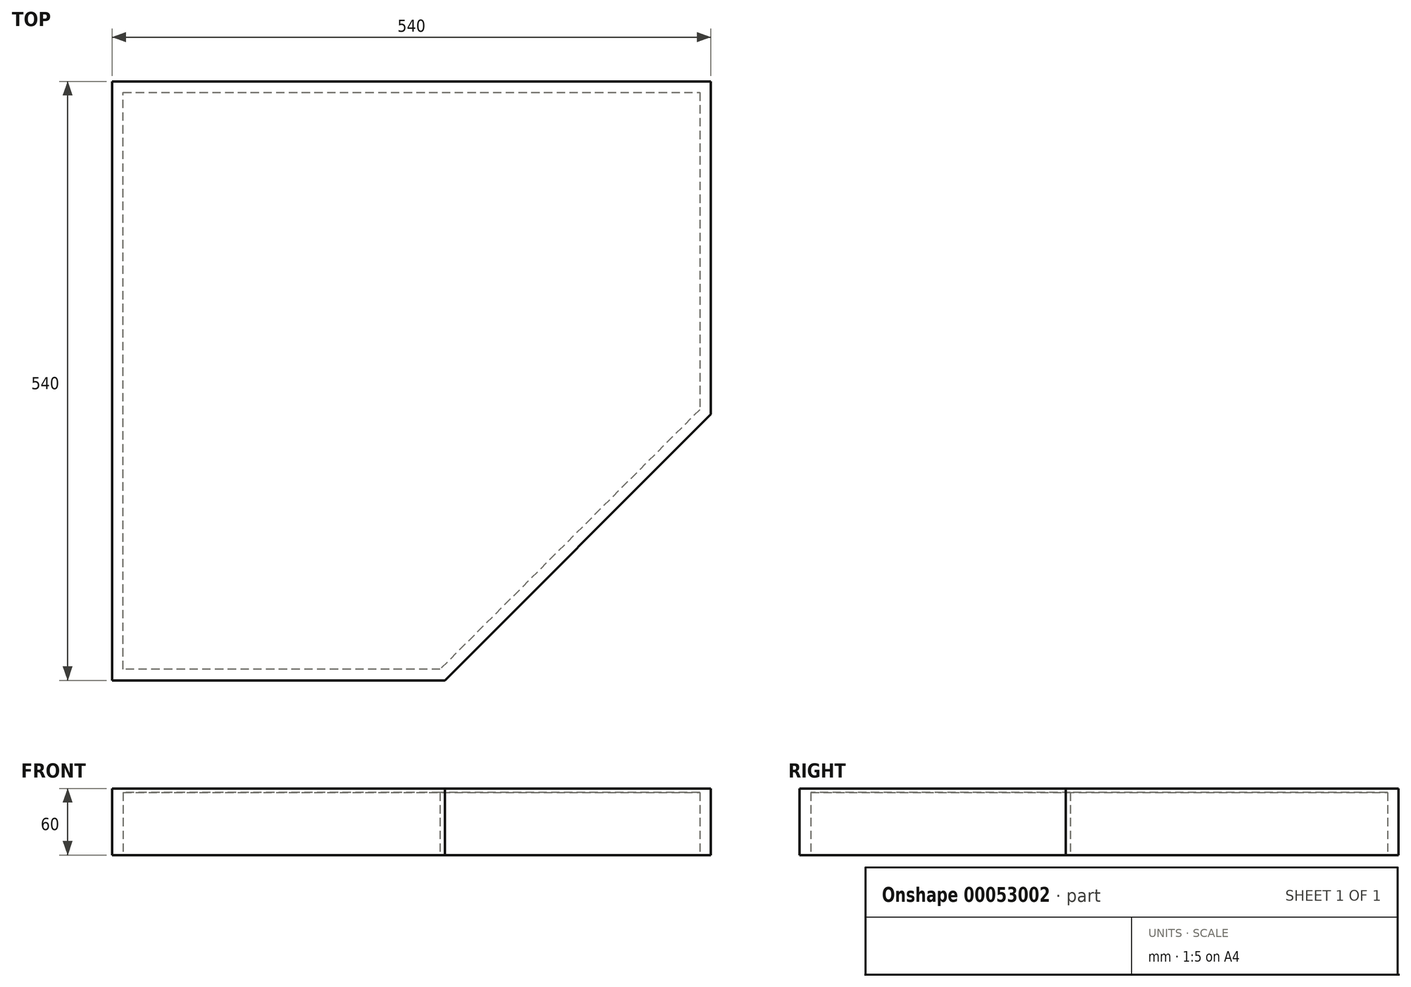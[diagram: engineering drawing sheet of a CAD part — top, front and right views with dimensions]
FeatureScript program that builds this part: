
annotation { "Feature Type Name" : "Feature", "Feature Type Description" : "" }
export const myFeature = defineFeature(function(context is Context, id is Id, definition is map)
    precondition{}
    {
        {
            var Q0;
            Q0=qCreatedBy(makeId("Top.planeOp"),FACE);
            var sketch = newSketch(context, id + "F0", { "sketchPlane" : qUnion([Q0])});
            skLineSegment(sketch, "E0.bottom", {"start": v(-270, 270) * mm, "end": v(270, 270) * mm});
            skLineSegment(sketch, "E0.top", {"start": v(-270, -270) * mm, "end": v(30, -270) * mm});
            skLineSegment(sketch, "E0.left", {"start": v(-270, 270) * mm, "end": v(-270, -270) * mm});
            skLineSegment(sketch, "E0.right", {"start": v(270, 270) * mm, "end": v(270, -30) * mm});
            skLineSegment(sketch, "E1", {"start": v(270, -30) * mm, "end": v(30, -270) * mm});
            skPoint(sketch, "E2", {"position": v(-270, 0) * mm});
            skPoint(sketch, "E3", {"position": v(0, 270) * mm});
            skSolve(sketch);
        }
        {
            var Q0;
            Q0=makeQuery(id+"F0.imprint","IMPRINT",FACE,{"disambiguationData":[TD([[makeQuery(id+"F0.imprint","IMPRINT",EDGE,{"derivedFrom":sQuery(id+"F0.wireOp",EDGE,"E0.bottom")}),-1.0]])]});
            extrude(context, id + "F1", {"entities" : qUnion([Q0]), "oppositeDirection" : true, "depth" : 3.6 * mm});
        }
        {
            var Q0;
            Q0=qCreatedBy(makeId("Top.planeOp"),FACE);
            cPlane(context, id + "F2", {"entities" : qUnion([Q0]), "cplaneType" : CPlaneType.OFFSET, "offset" : 60 * mm, "oppositeDirection" : true, "width" : 150 * mm, "height" : 150 * mm});
        }
        {
            var Q0;
            Q0=qCreatedBy(id+"F2.planeOp",FACE);
            var sketch = newSketch(context, id + "F3", { "sketchPlane" : qUnion([Q0])});
            skLineSegment(sketch, "E4.0.0", {"start": v(-270, 270) * mm, "end": v(270, 270) * mm});
            skLineSegment(sketch, "E4.0.1", {"start": v(270, 270) * mm, "end": v(270, -30) * mm});
            skLineSegment(sketch, "E4.0.2", {"start": v(270, -30) * mm, "end": v(30, -270) * mm});
            skLineSegment(sketch, "E4.0.3", {"start": v(30, -270) * mm, "end": v(-270, -270) * mm});
            skLineSegment(sketch, "E4.0.4", {"start": v(-270, -270) * mm, "end": v(-270, 270) * mm});
            skLineSegment(sketch, "E5.0", {"start": v(260, 260) * mm, "end": v(260, -25.86) * mm});
            skLineSegment(sketch, "E5.1", {"start": v(-260, 260) * mm, "end": v(260, 260) * mm});
            skLineSegment(sketch, "E5.2", {"start": v(260, -25.86) * mm, "end": v(25.86, -260) * mm});
            skLineSegment(sketch, "E5.3", {"start": v(25.86, -260) * mm, "end": v(-260, -260) * mm});
            skLineSegment(sketch, "E5.4", {"start": v(-260, -260) * mm, "end": v(-260, 260) * mm});
            skSolve(sketch);
        }
        {
            var Q0;
            Q0=makeQuery(id+"F3.imprint","IMPRINT",FACE,{"disambiguationData":[TD([[makeQuery(id+"F3.imprint","IMPRINT",EDGE,{"derivedFrom":sQuery(id+"F3.wireOp",EDGE,"E4.0.0")}),-1.0]])]});
            var Q1;
            Q1=makeQuery(id+"F1.opExtrude","CAP_FACE",FACE,{"disambiguationData":[OSD([sQuery(id+"F0.wireOp",EDGE,"E0.bottom"),sQuery(id+"F0.wireOp",EDGE,"E0.top"),sQuery(id+"F0.wireOp",EDGE,"E0.left"),sQuery(id+"F0.wireOp",EDGE,"E0.right"),sQuery(id+"F0.wireOp",EDGE,"E1")])],"isStart":false});
            extrude(context, id + "F4", {"entities" : qUnion([Q0]), "operationType" : NewBodyOperationType.ADD, "endBound" : BoundingType.UP_TO_SURFACE, "endBoundEntityFace" : qUnion([Q1]), "depth" : 25 * mm});
        }
    });
